# Revit family: Domotics-DomesticRanges-GEWISS-27COMBI_SYSTEM-IP40_4P+4P+4P_HORIZONTAL
name_source: partatom
category: Apparecchi elettrici
revit_build: Autodesk Revit 2016 (Build: 20161004_0715(x64)
units: mm (PartAtom-declared; Revit-internal decimal feet)

## family parameters
Condiviso = No
Host = Superficie
Mantenere orientamento annotazione = No
Numero OmniClass = 23.80.30.14.24
Punto di calcolo locali = No
Quota connettore circolare = Usa diametro
Taglio con vuoti quando caricato = Sì
Tipo di parte = Normale
Titolo OmniClass = Junction Boxes

## types (1)
- Domotics-DomesticRanges-GEWISS-27COMBI_SYSTEM-IP40_4P+4P+4P_HORIZONTAL
    Bidimensionale = bidimensionale system contenitori IP40 4X3P H : 4P
    Catalogue = DOMOTICS
    Catalogue Range = 27COMBI
    Characteristics = Halogen free
    Colour = Grey RAL 7035
    Compartment pre-arrangement = 3
    Configuration = Module 4 x 3
    Description: = 12 gang
    Descrizione = HORIZ.12(4X3) GANG ENCLOSURE IP40
    Dimensions LxHxD (mm) = 330x82x55
    EAN code = 8011564055308
    Electrocod = 0212
    Glow Wire Test = 650°C
    IDF = 4fa2526b-bcec-4f5e-b748-7f523d4194ae
    IDT = 0ac9fafb-c611-4cc4-9ad7-197cb8e27791
    IP degree = IP40
    Immagine tipo = GW27007.jpg
    Installation temperature = -25 +60 °C
    Insulation class = II
    Larghezza scatola = 330 mm  [stored 1.08268 ft]
    Lid screws = Corrosion-resistant steel
    Modello = GW27007
    No. knockout holes Ã˜ 23 = 16
    No. knockout holes Ã˜23 = 16 on sides / 3 on the bottom
    Outer dim. LxHxD (mm) = 330x82x55
    Produttore = GEWISS S.p.A.
    Prospetto di default = 1219 mm
    SCATOLA = GEWISS GRIGIO
    SEO = Enclosure
    Shock resistance = IK07
    Standard; = EN 60670-1
    Technical sheet = https://www.gewiss.com
    Thermo-pressure with ball = 70
    Tipo = SYSTEM CONTENITORI IP40 4X3P H_BASE : GW27007 - 4x3 posti orizzontali
    Torque screws tightening = 0,8NM
    Type of knockout holes = Removable with tool
    URL = https://www.gewiss.com
    Version file RFA = 19.4

note: source unit labels omitted for Thermo-pressure with ball — the stored unit's dimension contradicts the parameter name (converter mislabeling)

note: [stored X ft] marks values corroborated as IEEE doubles in the binary element streams (Revit-internal decimal feet)

## geometry (parser evidence)
native form markers: Blend x2
no freeform markers — native parametric forms only
